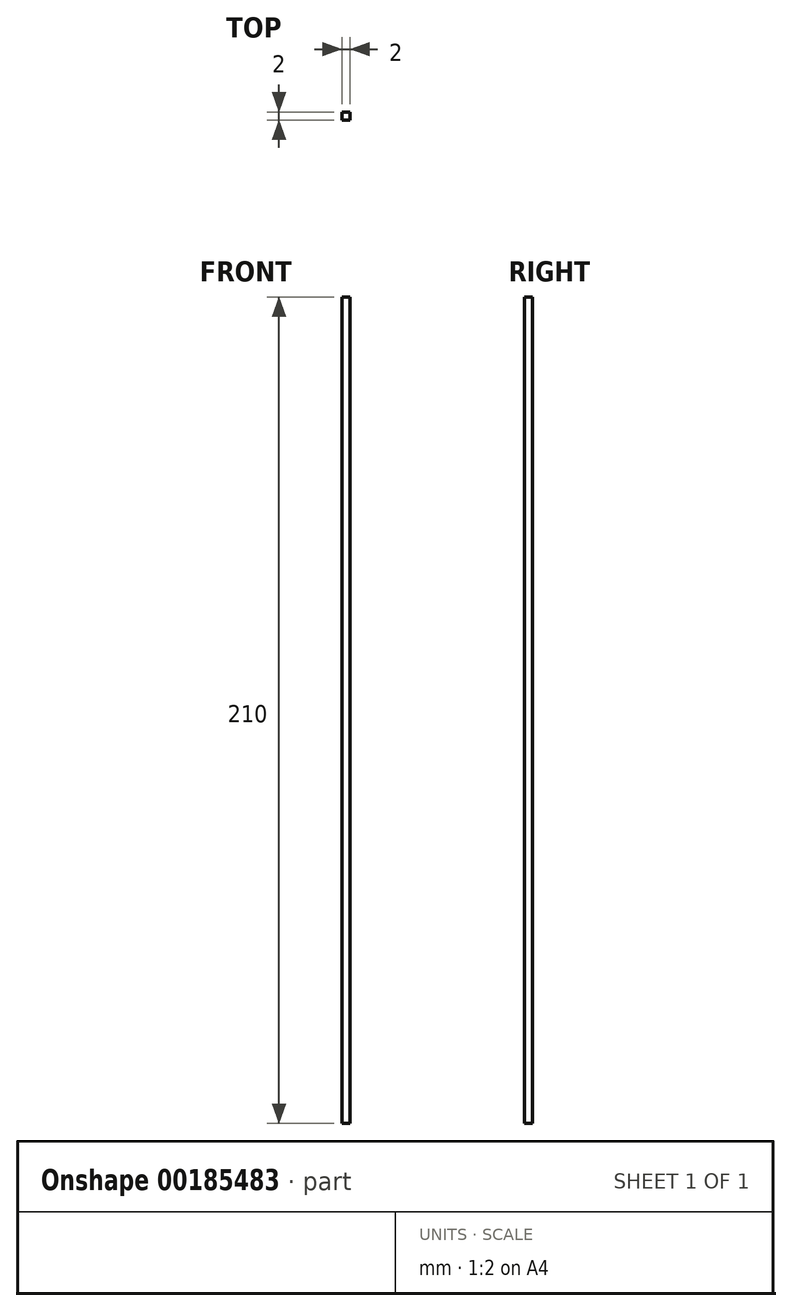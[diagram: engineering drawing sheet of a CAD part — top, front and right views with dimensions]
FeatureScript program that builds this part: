
annotation { "Feature Type Name" : "Feature", "Feature Type Description" : "" }
export const myFeature = defineFeature(function(context is Context, id is Id, definition is map)
    precondition{}
    {
        {
            var Q0;
            Q0=qCreatedBy(makeId("Top.planeOp"),FACE);
            var sketch = newSketch(context, id + "F0", { "sketchPlane" : qUnion([Q0])});
            skLineSegment(sketch, "E0.bottom", {"start": v(0, 0) * mm, "end": v(-2, 0) * mm});
            skLineSegment(sketch, "E0.top", {"start": v(0, 2) * mm, "end": v(-2, 2) * mm});
            skLineSegment(sketch, "E0.left", {"start": v(0, 0) * mm, "end": v(0, 2) * mm});
            skLineSegment(sketch, "E0.right", {"start": v(-2, 0) * mm, "end": v(-2, 2) * mm});
            skSolve(sketch);
        }
        {
            var Q0;
            Q0 = qSketchRegion(id + "F0", true);
            extrude(context, id + "F1", {"entities" : qUnion([Q0]), "depth" : 210 * mm});
        }
    });
